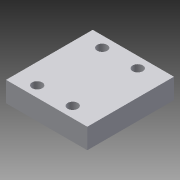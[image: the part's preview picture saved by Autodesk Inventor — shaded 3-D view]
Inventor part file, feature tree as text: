
AUTODESK INVENTOR PART (.ipt)
format: ipt  version: 2013 (Build 170138000, 138)  size: 88,064 bytes
history: native  units: mm
features: extrude x1, sketch x1
ambient origin geometry x8: Origin, YZ Plane, XZ Plane, XY Plane, X Axis, Y Axis, Z Axis, Center Point
bodies: Solid1 (feature_tree)
feature tree (2):
  extrude  "Extrusion1"  [1 undecoded]
  sketch  "Sketch1"  dims[d0=6.0mm d1=0.0mm]
note: 1 required parameter value undecoded (feature->parameter linkage not recoverable at this tier; creation-order binding heuristic only, values carry confidence <= 0.55)
